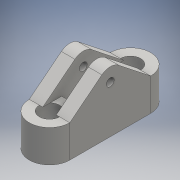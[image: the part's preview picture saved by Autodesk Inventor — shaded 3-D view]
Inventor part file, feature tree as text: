
AUTODESK INVENTOR PART (.ipt)
format: ipt  version: 2016 (Build 200138000, 138)  size: 162,304 bytes
history: native  units: mm
features: extrude x3, sketch x3, projected_geometry x3, mirror x1
ambient origin geometry x8: Origin, YZ Plane, XZ Plane, XY Plane, X Axis, Y Axis, Z Axis, Center Point
bodies: Solid1 (feature_tree)
feature tree (10):
  extrude  "Extrusion1"  Depth=30.0mm
  extrude  "Extrusion2"  Depth=30.0mm
  extrude  "Extrusion3"  Depth=10.0mm
  mirror  "Mirror1"
  sketch  "Sketch1"  dims[d0=30.0mm d1=6.1mm]
  sketch  "Sketch2"  dims[d2=15.0mm d3=30.0mm]
  projected_geometry  "Projected Loop1"
  sketch  "Sketch3"  dims[d4=24.0mm d5=0.0mm d6=10.0mm d7=32.0mm d8=14.0mm d9=0.0mm d10=25.0mm d11=5.8mm d12=10.0mm d13=14.0mm d14=0.0mm]
  projected_geometry  "Projected Loop2"
  projected_geometry  "Projected Loop3"
